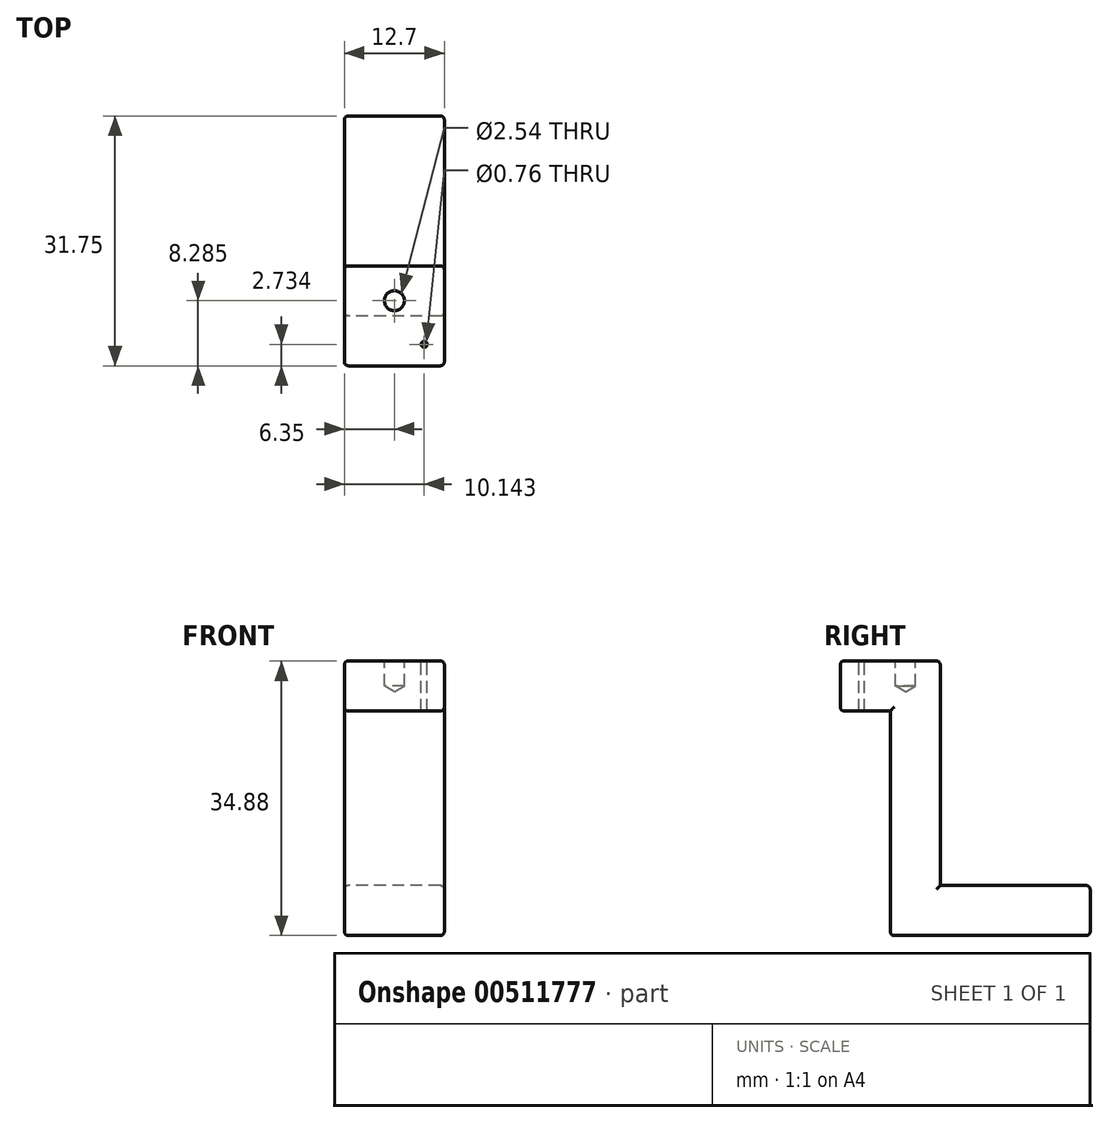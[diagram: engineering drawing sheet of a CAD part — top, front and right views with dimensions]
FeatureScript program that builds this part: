
annotation { "Feature Type Name" : "Feature", "Feature Type Description" : "" }
export const myFeature = defineFeature(function(context is Context, id is Id, definition is map)
    precondition{}
    {
        {
            var Q0;
            Q0=qCreatedBy(makeId("Right.planeOp"),FACE);
            var sketch = newSketch(context, id + "F0", { "sketchPlane" : qUnion([Q0])});
            skLineSegment(sketch, "E0", {"start": v(-23.4, 24.17) * mm, "end": v(-10.7, 24.17) * mm});
            skLineSegment(sketch, "E1", {"start": v(-10.7, 24.17) * mm, "end": v(-10.7, -4.36) * mm});
            skLineSegment(sketch, "E2", {"start": v(-10.7, -4.36) * mm, "end": v(8.34, -4.36) * mm});
            skLineSegment(sketch, "E3", {"start": v(8.34, -4.36) * mm, "end": v(8.34, -10.7) * mm});
            skLineSegment(sketch, "E4", {"start": v(8.34, -10.7) * mm, "end": v(-17.06, -10.7) * mm});
            skLineSegment(sketch, "E5", {"start": v(-17.06, -10.7) * mm, "end": v(-17.06, 17.82) * mm});
            skLineSegment(sketch, "E6", {"start": v(-17.06, 17.82) * mm, "end": v(-23.4, 17.82) * mm});
            skLineSegment(sketch, "E7", {"start": v(-23.4, 24.17) * mm, "end": v(-23.4, 17.82) * mm});
            skSolve(sketch);
        }
        {
            var Q0;
            Q0=makeQuery(id+"F0.imprint","IMPRINT",FACE,{"disambiguationData":[TD([[makeQuery(id+"F0.imprint","IMPRINT",EDGE,{"derivedFrom":sQuery(id+"F0.wireOp",EDGE,"E0")}),-1.0]])]});
            extrude(context, id + "F1", {"entities" : qUnion([Q0]), "depth" : 6.35 * mm, "hasSecondDirection" : true, "secondDirectionOppositeDirection" : true, "secondDirectionDepth" : 6.35 * mm});
        }
        {
            var Q0;
            Q0=makeQuery(id+"F1.opExtrude","SWEPT_EDGE",EDGE,{"disambiguationData":[OSD([sQuery(id+"F0.wireOp",EDGE,"E0"),sQuery(id+"F0.wireOp",EDGE,"E7")])]});
            var Q1;
            Q1=makeQuery(id+"F1.opExtrude","CAP_EDGE",EDGE,{"disambiguationData":[OSD([sQuery(id+"F0.wireOp",EDGE,"E0")])],"isStart":false});
            var Q2;
            Q2=makeQuery(id+"F1.opExtrude","SWEPT_EDGE",EDGE,{"disambiguationData":[OSD([sQuery(id+"F0.wireOp",EDGE,"E0"),sQuery(id+"F0.wireOp",EDGE,"E1")])]});
            var Q3;
            Q3=makeQuery(id+"F1.opExtrude","CAP_EDGE",EDGE,{"disambiguationData":[OSD([sQuery(id+"F0.wireOp",EDGE,"E0")])],"isStart":true});
            fillet(context, id + "F2", {"entities" : qUnion([Q0, Q1, Q2, Q3]), "radius" : 0.5 * mm, "tangentPropagation" : true, "allowEdgeOverflow" : false});
        }
        {
            var Q0;
            Q0=makeQuery(id+"F1.opExtrude","CAP_EDGE",EDGE,{"disambiguationData":[OSD([sQuery(id+"F0.wireOp",EDGE,"E7")])],"isStart":false});
            var Q1;
            Q1=makeQuery(id+"F1.opExtrude","CAP_EDGE",EDGE,{"disambiguationData":[OSD([sQuery(id+"F0.wireOp",EDGE,"E6")])],"isStart":false});
            var Q2;
            Q2=makeQuery(id+"F1.opExtrude","CAP_EDGE",EDGE,{"disambiguationData":[OSD([sQuery(id+"F0.wireOp",EDGE,"E1")])],"isStart":false});
            var Q3;
            Q3=makeQuery(id+"F1.opExtrude","CAP_EDGE",EDGE,{"disambiguationData":[OSD([sQuery(id+"F0.wireOp",EDGE,"E5")])],"isStart":false});
            var Q4;
            Q4=makeQuery(id+"F1.opExtrude","CAP_EDGE",EDGE,{"disambiguationData":[OSD([sQuery(id+"F0.wireOp",EDGE,"E4")])],"isStart":false});
            var Q5;
            Q5=makeQuery(id+"F1.opExtrude","CAP_EDGE",EDGE,{"disambiguationData":[OSD([sQuery(id+"F0.wireOp",EDGE,"E2")])],"isStart":false});
            var Q6;
            Q6=makeQuery(id+"F1.opExtrude","CAP_EDGE",EDGE,{"disambiguationData":[OSD([sQuery(id+"F0.wireOp",EDGE,"E3")])],"isStart":false});
            fillet(context, id + "F3", {"entities" : qUnion([Q0, Q1, Q2, Q3, Q4, Q5, Q6]), "radius" : 0.5 * mm, "tangentPropagation" : true, "allowEdgeOverflow" : false});
        }
        {
            var Q0;
            Q0=makeQuery(id+"F1.opExtrude","CAP_EDGE",EDGE,{"disambiguationData":[OSD([sQuery(id+"F0.wireOp",EDGE,"E1")])],"isStart":true});
            var Q1;
            Q1=makeQuery(id+"F1.opExtrude","SWEPT_EDGE",EDGE,{"disambiguationData":[OSD([sQuery(id+"F0.wireOp",EDGE,"E2"),sQuery(id+"F0.wireOp",EDGE,"E3")])]});
            var Q2;
            Q2=makeQuery(id+"F1.opExtrude","SWEPT_EDGE",EDGE,{"disambiguationData":[OSD([sQuery(id+"F0.wireOp",EDGE,"E3"),sQuery(id+"F0.wireOp",EDGE,"E4")])]});
            var Q3;
            Q3=makeQuery(id+"F1.opExtrude","CAP_EDGE",EDGE,{"disambiguationData":[OSD([sQuery(id+"F0.wireOp",EDGE,"E3")])],"isStart":true});
            var Q4;
            Q4=makeQuery(id+"F1.opExtrude","CAP_EDGE",EDGE,{"disambiguationData":[OSD([sQuery(id+"F0.wireOp",EDGE,"E4")])],"isStart":true});
            var Q5;
            Q5=makeQuery(id+"F1.opExtrude","CAP_EDGE",EDGE,{"disambiguationData":[OSD([sQuery(id+"F0.wireOp",EDGE,"E5")])],"isStart":true});
            var Q6;
            Q6=makeQuery(id+"F1.opExtrude","CAP_EDGE",EDGE,{"disambiguationData":[OSD([sQuery(id+"F0.wireOp",EDGE,"E2")])],"isStart":true});
            var Q7;
            Q7=makeQuery(id+"F1.opExtrude","CAP_EDGE",EDGE,{"disambiguationData":[OSD([sQuery(id+"F0.wireOp",EDGE,"E6")])],"isStart":true});
            var Q8;
            Q8=makeQuery(id+"F1.opExtrude","CAP_EDGE",EDGE,{"disambiguationData":[OSD([sQuery(id+"F0.wireOp",EDGE,"E7")])],"isStart":true});
            fillet(context, id + "F4", {"entities" : qUnion([Q0, Q1, Q2, Q3, Q4, Q5, Q6, Q7, Q8]), "radius" : 0.5 * mm, "tangentPropagation" : true, "allowEdgeOverflow" : false});
        }
        {
            var Q0;
            Q0=makeQuery(id+"F1.opExtrude","SWEPT_EDGE",EDGE,{"disambiguationData":[OSD([sQuery(id+"F0.wireOp",EDGE,"E4"),sQuery(id+"F0.wireOp",EDGE,"E5")])]});
            fillet(context, id + "F5", {"entities" : qUnion([Q0]), "radius" : 0.5 * mm, "tangentPropagation" : true, "allowEdgeOverflow" : false});
        }
        {
            var Q0;
            Q0=makeQuery(id+"F1.opExtrude","SWEPT_EDGE",EDGE,{"disambiguationData":[OSD([sQuery(id+"F0.wireOp",EDGE,"E6"),sQuery(id+"F0.wireOp",EDGE,"E7")])]});
            fillet(context, id + "F6", {"entities" : qUnion([Q0]), "radius" : 0.5 * mm, "tangentPropagation" : true, "allowEdgeOverflow" : false});
        }
        {
            var Q0;
            Q0=makeQuery(id+"F1.opExtrude","SWEPT_FACE",FACE,{"disambiguationData":[OSD([sQuery(id+"F0.wireOp",EDGE,"E0")])]});
            var sketch = newSketch(context, id + "F7", { "sketchPlane" : qUnion([Q0])});
            skPoint(sketch, "E8", {"position": v(0, -15.12) * mm});
            skPoint(sketch, "E9", {"position": v(3.38, -20.26) * mm});
            skSolve(sketch);
        }
        {
            var Q0;
            Q0=sQuery(id+"F7.wireOp",VERTEX,"E8");
            var Q1;
            Q1=makeQuery(id+"F1.opExtrude","SWEPT_BODY",BODY,{"disambiguationData":[OSD([sQuery(id+"F0.wireOp",EDGE,"E0"),sQuery(id+"F0.wireOp",EDGE,"E1"),sQuery(id+"F0.wireOp",EDGE,"E2"),sQuery(id+"F0.wireOp",EDGE,"E3"),sQuery(id+"F0.wireOp",EDGE,"E4"),sQuery(id+"F0.wireOp",EDGE,"E5"),sQuery(id+"F0.wireOp",EDGE,"E6"),sQuery(id+"F0.wireOp",EDGE,"E7")])]});
            hole(context, id + "F8", {"style" : HoleStyle.SIMPLE, "endStyle" : HoleEndStyle.BLIND, "holeDiameter" : 2.54 * mm, "holeDepth" : 3.17 * mm, "isTappedThrough" : true, "tappedDepth" : 12.7 * mm, "tapClearance" : 3, "locations" : qUnion([Q0]), "scope" : qUnion([Q1])});
        }
        {
            var Q0;
            Q0=makeQuery(id+"F1.opExtrude","SWEPT_FACE",FACE,{"disambiguationData":[OSD([sQuery(id+"F0.wireOp",EDGE,"E0")])]});
            var sketch = newSketch(context, id + "F9", { "sketchPlane" : qUnion([Q0])});
            skPoint(sketch, "E10", {"position": v(3.8, -20.68) * mm});
            skSolve(sketch);
        }
        {
            var Q0;
            Q0=sQuery(id+"F9.wireOp",VERTEX,"E10");
            var Q1;
            Q1=makeQuery(id+"F1.opExtrude","SWEPT_BODY",BODY,{"disambiguationData":[OSD([sQuery(id+"F0.wireOp",EDGE,"E0"),sQuery(id+"F0.wireOp",EDGE,"E1"),sQuery(id+"F0.wireOp",EDGE,"E2"),sQuery(id+"F0.wireOp",EDGE,"E3"),sQuery(id+"F0.wireOp",EDGE,"E4"),sQuery(id+"F0.wireOp",EDGE,"E5"),sQuery(id+"F0.wireOp",EDGE,"E6"),sQuery(id+"F0.wireOp",EDGE,"E7")])]});
            hole(context, id + "F10", {"style" : HoleStyle.SIMPLE, "endStyle" : HoleEndStyle.THROUGH, "holeDiameter" : 0.76 * mm, "isTappedThrough" : true, "tappedDepth" : 12.7 * mm, "tapClearance" : 3, "locations" : qUnion([Q0]), "scope" : qUnion([Q1])});
        }
    });
